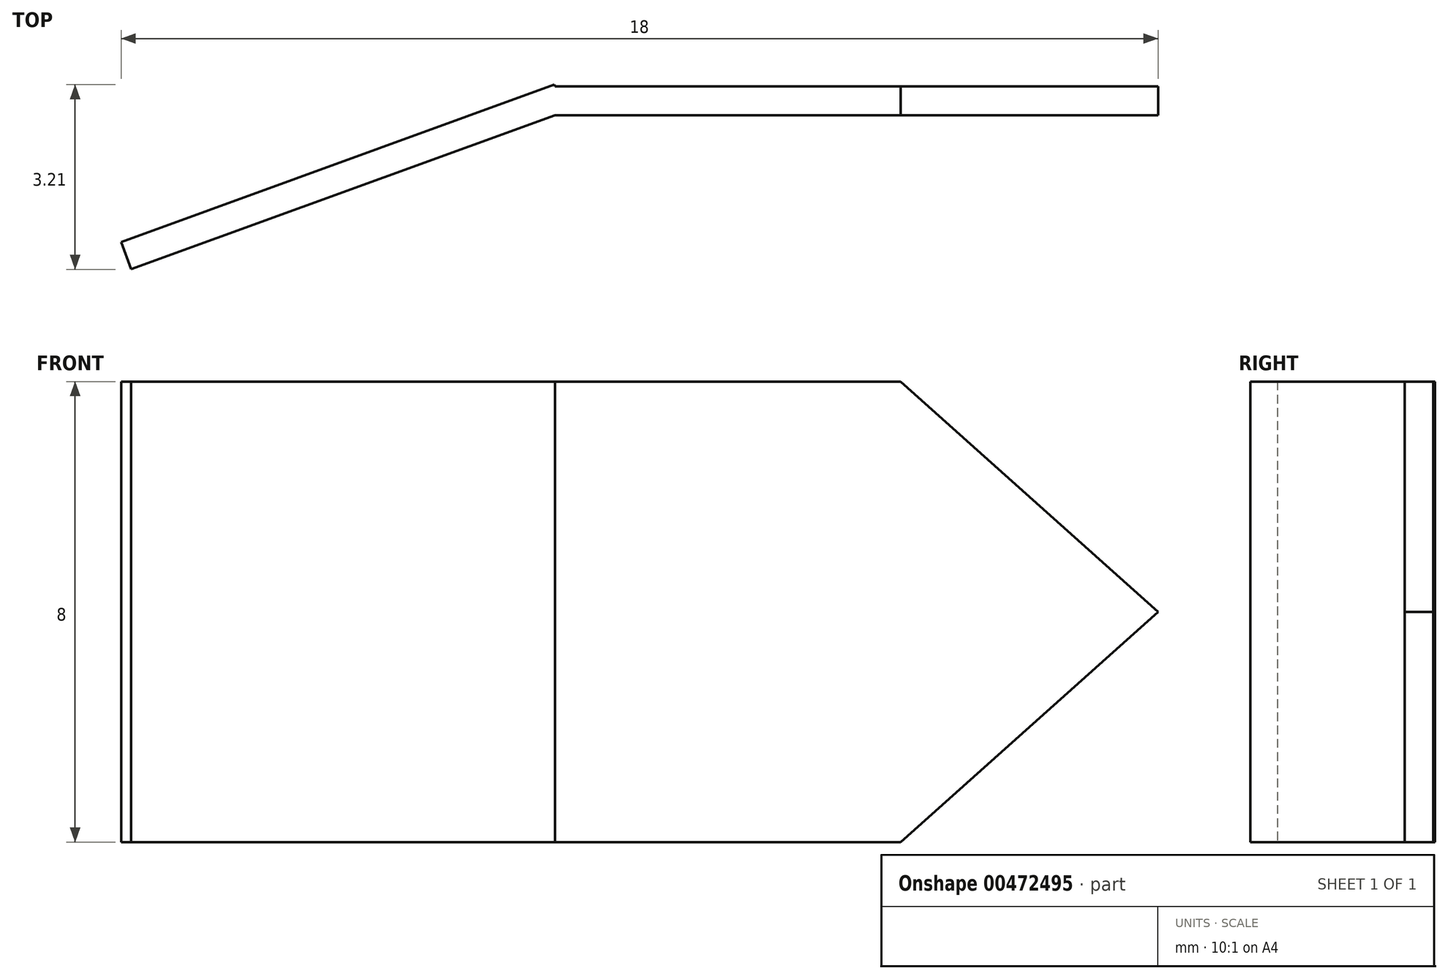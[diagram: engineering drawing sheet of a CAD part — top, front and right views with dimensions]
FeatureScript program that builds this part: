
annotation { "Feature Type Name" : "Feature", "Feature Type Description" : "" }
export const myFeature = defineFeature(function(context is Context, id is Id, definition is map)
    precondition{}
    {
        {
            var Q0;
            Q0=qCreatedBy(makeId("Front.planeOp"),FACE);
            var sketch = newSketch(context, id + "F0", { "sketchPlane" : qUnion([Q0])});
            skLineSegment(sketch, "E0", {"start": v(0, 0) * mm, "end": v(0, -8) * mm});
            skLineSegment(sketch, "E1", {"start": v(0, -8) * mm, "end": v(6, -8) * mm});
            skLineSegment(sketch, "E2", {"start": v(6, -8) * mm, "end": v(10.47, -4) * mm});
            skLineSegment(sketch, "E3", {"start": v(10.47, -4) * mm, "end": v(6, 0) * mm});
            skLineSegment(sketch, "E4", {"start": v(6, 0) * mm, "end": v(0, 0) * mm});
            skSolve(sketch);
        }
        {
            var Q0;
            Q0 = qSketchRegion(id + "F0", true);
            extrude(context, id + "F1", {"entities" : qUnion([Q0]), "depth" : 0.5 * mm});
        }
        {
            var Q0;
            Q0=makeQuery(id+"F1.opExtrude","SWEPT_FACE",FACE,{"disambiguationData":[OSD([sQuery(id+"F0.wireOp",EDGE,"E0")])]});
            var Q1;
            Q1=makeQuery(id+"F1.opExtrude","CAP_EDGE",EDGE,{"disambiguationData":[OSD([sQuery(id+"F0.wireOp",EDGE,"E0")])],"isStart":false});
            cPlane(context, id + "F2", {"entities" : qUnion([Q0, Q1]), "cplaneType" : CPlaneType.LINE_ANGLE, "offset" : 0 * mm, "angle" : 70 * degree, "width" : 150 * mm, "height" : 150 * mm});
        }
        {
            var Q0;
            Q0=qCreatedBy(id+"F2.planeOp",FACE);
            var sketch = newSketch(context, id + "F3", { "sketchPlane" : qUnion([Q0])});
            skLineSegment(sketch, "E5", {"start": v(0, 0) * mm, "end": v(-8, 0) * mm});
            skLineSegment(sketch, "E6", {"start": v(-8, 0) * mm, "end": v(-8, -8) * mm});
            skLineSegment(sketch, "E7", {"start": v(-8, -8) * mm, "end": v(0, -8) * mm});
            skLineSegment(sketch, "E8", {"start": v(0, 0) * mm, "end": v(0, -8) * mm});
            skSolve(sketch);
        }
        {
            var Q0;
            Q0=makeQuery(id+"F3.imprint","IMPRINT",FACE,{"disambiguationData":[TD([[makeQuery(id+"F3.imprint","IMPRINT",EDGE,{"derivedFrom":sQuery(id+"F3.wireOp",EDGE,"E5")}),1.0]])]});
            extrude(context, id + "F4", {"entities" : qUnion([Q0]), "operationType" : NewBodyOperationType.ADD, "oppositeDirection" : true, "depth" : 0.5 * mm});
        }
    });
